# Revit family: ElectricalFixture_WiringAccessories_Hager_Sollysta_2Gang
name_source: partatom
category: Lighting Fixtures
revit_build: Autodesk Revit 2015 (Build: 20160512_1515(x64)
units: mm (PartAtom-declared; Revit-internal decimal feet)

## types (2) — shared parameters
AssetType = Fixed
Back Plate Depth = 10 mm  [stored 0.0328084 ft]
Back Plate Height = 59 mm
Back Plate Width = 25 mm  [stored 0.082021 ft]
Category = ElectricalFixture
ClassificationName = Uniclass2015
ClassificationValue = Pr_65_72_97
Colour = RAL9010WhiteGloss
Default Elevation = 500 mm  [stored 1.64042 ft]
DocumentationCertificates = http://www.hager.co.uk
DocumentationLiterature = http://www.hager.co.uk
DocumentationTechnical = http://www.hager.co.uk
DurationUnit = Years
ExpectedLife = 25
Flex Outlet = No
Frequency = 50/60Hz
IfcExportAs = ElectricalFixture
IfcExportType = ElectricalFixture
Keynote = 16400
LED Indicator Switch = No
Manufacturer = Hager
ManufacturerName = Hager
Material = Urea Formaldehyde Thermoset Plastic
NBSDescription = ElectricalFixture
NBSReference = Pr_65_72_97
NominalHeight = 86 mm  [stored 0.282152 ft]
NominalLength = 86 mm  [stored 0.282152 ft]
NominalWidth = 7 mm  [stored 0.0229659 ft]
One Way = No
Shape = Rectangular
Supply Phase = 1
Switch = Yes
Switch Height = 33 mm
Switch Width = 17 mm
Two Way = Yes
URL = http://www.hager.co.uk
Voltage = 230V/240V
WarrantyDescription = See Manufacturer
WarrantyDurationParts = 10
WarrantyDurationUnit = Years
WarrantyGuarantorParts = 10
_BimstoreBibleVersion = V14
_DistributedBy = www.bimstore.co.uk
zero-valued in all types: ReplacementCost, ServiceLifeDuration, WarrantyDurationLabor, _BimSpecGuid, _CurrentRevision

## per-type parameters (varying)
| type | BIMObjectName | Description | Double Switch | EAN | Extrusion From Wall | Features | NBSObjectName | NominalDepth | TypeName | Wide Rocker |
| WMPS22 | Hager_ElectricalFixture_WMPS22 | 10AX2Gang2WayWallSwitch | Yes | 5015652260820 | 7 mm  [stored 0.0229659 ft] | 10AX2Gang2WayWallSwitch | Hager_10AXWallSwitches_WMPS22 | 18 mm | ElectricalFixture_10AXWallSwitches_WMPS22 | No |
| WMPS22W | Hager_ElectricalFixture_WMPS22W | 10AX2Gang2WayWallSwitchWideRocker | No | 5015652261742 | 12 mm  [stored 0.0393701 ft] | 10AX2Gang2WayWallSwitchWideRocker | Hager_10AXWallSwitches_WMPS22W | 22 mm | ElectricalFixture_10AXWallSwitches_WMPS22W | Yes |

note: column(s) folded — value = type name in every type: Model, ModelNumber, ModelReference, Type Comments

note: [stored X ft] marks values corroborated as IEEE doubles in the binary element streams (Revit-internal decimal feet)

## geometry (parser evidence)
native form markers: Blend x4, Sweep x3
no freeform markers — native parametric forms only
